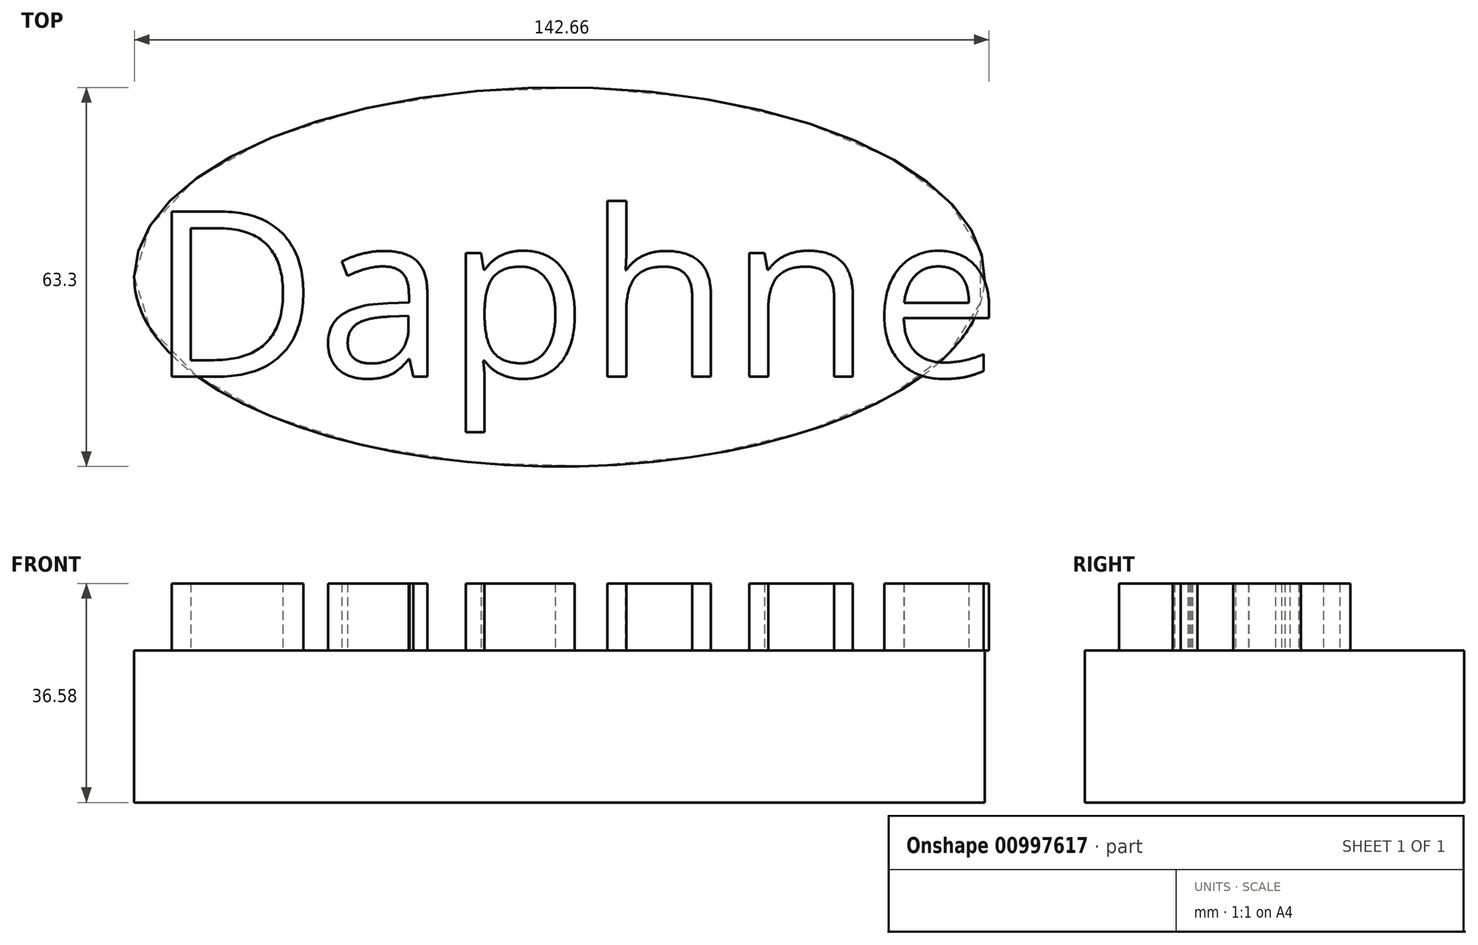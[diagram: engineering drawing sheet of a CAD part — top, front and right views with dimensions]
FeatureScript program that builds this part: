
annotation { "Feature Type Name" : "Feature", "Feature Type Description" : "" }
export const myFeature = defineFeature(function(context is Context, id is Id, definition is map)
    precondition{}
    {
        {
            var Q0;
            Q0=qCreatedBy(makeId("Top.planeOp"),FACE);
            var sketch = newSketch(context, id + "F0", { "sketchPlane" : qUnion([Q0])});
            skEllipse(sketch, "E0", {"center": v(0, 0) * mm, "majorRadius": 70.97 * mm, "minorRadius": 31.65 * mm, "majorAxis": v(-1, 0)});
            skSolve(sketch);
        }
        {
            var Q0;
            Q0=makeQuery(id+"F0.imprint","IMPRINT",FACE,{"disambiguationData":[TD([[makeQuery(id+"F0.imprint","IMPRINT",EDGE,{"derivedFrom":sQuery(id+"F0.wireOp",EDGE,"E0")}),1.0]])]});
            extrude(context, id + "F1", {"entities" : qUnion([Q0]), "depth" : 25.4 * mm, "offsetDistance" : 25.4 * mm});
        }
        {
            var Q0;
            Q0=makeQuery(id+"F1.opExtrude","CAP_FACE",FACE,{"disambiguationData":[OSD([sQuery(id+"F0.wireOp",EDGE,"E0")])],"isStart":false});
            var sketch = newSketch(context, id + "F2", { "sketchPlane" : qUnion([Q0])});
            skText(sketch, "E1", { "text": "Daphne", "fontName": "OpenSans-Regular.ttf"});
            const initialGuessF2  = {"E1": [-0.06853, -0.01664, 1, 0, 0.02778]};
            skSetInitialGuess(sketch, initialGuessF2);
            skSolve(sketch);
        }
        {
            var Q0;
            Q0 = qSketchRegion(id + "F2", true);
            extrude(context, id + "F3", {"entities" : qUnion([Q0]), "operationType" : NewBodyOperationType.ADD, "depth" : 11.18 * mm, "offsetDistance" : 25.4 * mm});
        }
    });
